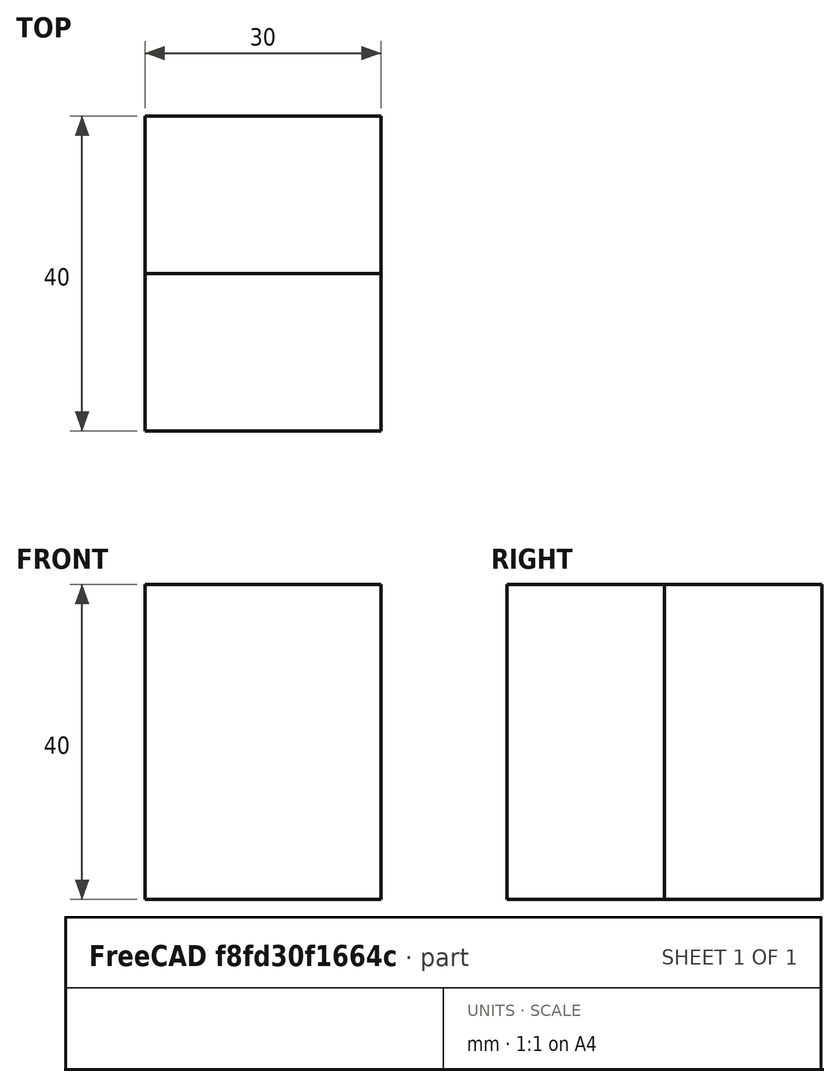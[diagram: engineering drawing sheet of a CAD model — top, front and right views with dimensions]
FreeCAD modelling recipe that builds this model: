
FCSTD DOCUMENT  (FreeCAD 0.17R13509 (Git))
Label: tensor
License: All rights reserved
LicenseURL: http://en.wikipedia.org/wiki/All_rights_reserved
objects: Part::Box×48, Part::MultiFuse×22
note: 70 computed .brp shape members not serialized (recipe doc carries the construction recipe); baked Part::Feature solids carry a one-line shape summary decoded from their .brp

FEATURE [Part::Box] Box021  label="Cube021"
  AttacherType = Attacher::AttachEngine3D
  Height = 10
  Length = 10
  Placement = pos=(34,0,30) rot=(0,0,1;0rad)
  Width = 10
FEATURE [Part::Box] Box022  label="Cube022"
  AttacherType = Attacher::AttachEngine3D
  Height = 10
  Length = 10
  Placement = pos=(14,0,30) rot=(0,0,1;0rad)
  Width = 10
FEATURE [Part::Box] Box023  label="Cube023"
  AttacherType = Attacher::AttachEngine3D
  Height = 10
  Length = 10
  Placement = pos=(14,0,30) rot=(0,0,1;0rad)
  Width = 10
FEATURE [Part::Box] Box024  label="Cube024"
  AttacherType = Attacher::AttachEngine3D
  Height = 10
  Length = 10
  Placement = pos=(24,0,30) rot=(0,0,1;0rad)
  Width = 10
FEATURE [Part::Box] Box025  label="Cube025"
  AttacherType = Attacher::AttachEngine3D
  Height = 10
  Length = 10
  Placement = pos=(24,0,30) rot=(0,0,1;0rad)
  Width = 10
FEATURE [Part::MultiFuse] Fusion012
  Shapes = -> [Box022,Box025,Box021]
FEATURE [Part::Box] Box026  label="Cube026"
  AttacherType = Attacher::AttachEngine3D
  Height = 10
  Length = 10
  Placement = pos=(34,0,30) rot=(0,0,1;0rad)
  Width = 10
FEATURE [Part::MultiFuse] Fusion011
  Placement = pos=(0,0,-10) rot=(0,0,1;0rad)
  Shapes = -> [Box023,Box024,Box026]
FEATURE [Part::Box] Box027  label="Cube027"
  AttacherType = Attacher::AttachEngine3D
  Height = 10
  Length = 10
  Placement = pos=(34,0,30) rot=(0,0,1;0rad)
  Width = 10
FEATURE [Part::Box] Box028  label="Cube028"
  AttacherType = Attacher::AttachEngine3D
  Height = 10
  Length = 10
  Placement = pos=(14,0,30) rot=(0,0,1;0rad)
  Width = 10
FEATURE [Part::Box] Box029  label="Cube029"
  AttacherType = Attacher::AttachEngine3D
  Height = 10
  Length = 10
  Placement = pos=(24,0,30) rot=(0,0,1;0rad)
  Width = 10
FEATURE [Part::MultiFuse] Fusion008
  Placement = pos=(0,0,-20) rot=(0,0,1;0rad)
  Shapes = -> [Box028,Box029,Box027]
FEATURE [Part::Box] Box030  label="Cube030"
  AttacherType = Attacher::AttachEngine3D
  Height = 10
  Length = 10
  Placement = pos=(34,0,30) rot=(0,0,1;0rad)
  Width = 10
FEATURE [Part::Box] Box031  label="Cube031"
  AttacherType = Attacher::AttachEngine3D
  Height = 10
  Length = 10
  Placement = pos=(14,0,30) rot=(0,0,1;0rad)
  Width = 10
FEATURE [Part::Box] Box032  label="Cube032"
  AttacherType = Attacher::AttachEngine3D
  Height = 10
  Length = 10
  Placement = pos=(24,0,30) rot=(0,0,1;0rad)
  Width = 10
FEATURE [Part::MultiFuse] Fusion009
  Placement = pos=(0,0,-30) rot=(0,0,1;0rad)
  Shapes = -> [Box031,Box032,Box030]
FEATURE [Part::MultiFuse] Fusion010  label="Mode013"
  Placement = pos=(0,-14,0) rot=(0,0,1;0rad)
  Shapes = -> [Fusion012,Fusion011,Fusion009,Fusion008]
FEATURE [Part::Box] Box033  label="Cube033"
  AttacherType = Attacher::AttachEngine3D
  Height = 10
  Length = 10
  Placement = pos=(34,0,30) rot=(0,0,1;0rad)
  Width = 10
FEATURE [Part::Box] Box034  label="Cube034"
  AttacherType = Attacher::AttachEngine3D
  Height = 10
  Length = 10
  Placement = pos=(24,0,30) rot=(0,0,1;0rad)
  Width = 10
FEATURE [Part::Box] Box035  label="Cube035"
  AttacherType = Attacher::AttachEngine3D
  Height = 10
  Length = 10
  Placement = pos=(14,0,30) rot=(0,0,1;0rad)
  Width = 10
FEATURE [Part::Box] Box036  label="Cube036"
  AttacherType = Attacher::AttachEngine3D
  Height = 10
  Length = 10
  Placement = pos=(14,0,30) rot=(0,0,1;0rad)
  Width = 10
FEATURE [Part::Box] Box037  label="Cube037"
  AttacherType = Attacher::AttachEngine3D
  Height = 10
  Length = 10
  Placement = pos=(34,0,30) rot=(0,0,1;0rad)
  Width = 10
FEATURE [Part::Box] Box038  label="Cube038"
  AttacherType = Attacher::AttachEngine3D
  Height = 10
  Length = 10
  Placement = pos=(14,0,30) rot=(0,0,1;0rad)
  Width = 10
FEATURE [Part::Box] Box039  label="Cube039"
  AttacherType = Attacher::AttachEngine3D
  Height = 10
  Length = 10
  Placement = pos=(24,0,30) rot=(0,0,1;0rad)
  Width = 10
FEATURE [Part::Box] Box040  label="Cube040"
  AttacherType = Attacher::AttachEngine3D
  Height = 10
  Length = 10
  Placement = pos=(14,0,30) rot=(0,0,1;0rad)
  Width = 10
FEATURE [Part::MultiFuse] Fusion016
  Placement = pos=(0,0,-20) rot=(0,0,1;0rad)
  Shapes = -> [Box040,Box034,Box033]
FEATURE [Part::Box] Box041  label="Cube041"
  AttacherType = Attacher::AttachEngine3D
  Height = 10
  Length = 10
  Placement = pos=(24,0,30) rot=(0,0,1;0rad)
  Width = 10
FEATURE [Part::Box] Box042  label="Cube042"
  AttacherType = Attacher::AttachEngine3D
  Height = 10
  Length = 10
  Placement = pos=(34,0,30) rot=(0,0,1;0rad)
  Width = 10
FEATURE [Part::MultiFuse] Fusion013
  Placement = pos=(0,0,-30) rot=(0,0,1;0rad)
  Shapes = -> [Box036,Box039,Box042]
FEATURE [Part::Box] Box043  label="Cube043"
  AttacherType = Attacher::AttachEngine3D
  Height = 10
  Length = 10
  Placement = pos=(34,0,30) rot=(0,0,1;0rad)
  Width = 10
FEATURE [Part::MultiFuse] Fusion015
  Shapes = -> [Box038,Box041,Box043]
FEATURE [Part::Box] Box044  label="Cube044"
  AttacherType = Attacher::AttachEngine3D
  Height = 10
  Length = 10
  Placement = pos=(24,0,30) rot=(0,0,1;0rad)
  Width = 10
FEATURE [Part::MultiFuse] Fusion017
  Placement = pos=(0,0,-10) rot=(0,0,1;0rad)
  Shapes = -> [Box035,Box044,Box037]
FEATURE [Part::MultiFuse] Fusion014  label="Mode014"
  Placement = pos=(0,-24,0) rot=(0,0,1;0rad)
  Shapes = -> [Fusion015,Fusion017,Fusion013,Fusion016]
FEATURE [Part::MultiFuse] Fusion  label="Mode123"
  Shapes = -> [Fusion014,Fusion010]
FEATURE [Part::Box] Box045  label="Cube045"
  AttacherType = Attacher::AttachEngine3D
  Height = 10
  Length = 10
  Placement = pos=(34,0,30) rot=(0,0,1;0rad)
  Width = 10
FEATURE [Part::Box] Box046  label="Cube046"
  AttacherType = Attacher::AttachEngine3D
  Height = 10
  Length = 10
  Placement = pos=(14,0,30) rot=(0,0,1;0rad)
  Width = 10
FEATURE [Part::Box] Box047  label="Cube047"
  AttacherType = Attacher::AttachEngine3D
  Height = 10
  Length = 10
  Placement = pos=(14,0,30) rot=(0,0,1;0rad)
  Width = 10
FEATURE [Part::Box] Box048  label="Cube048"
  AttacherType = Attacher::AttachEngine3D
  Height = 10
  Length = 10
  Placement = pos=(24,0,30) rot=(0,0,1;0rad)
  Width = 10
FEATURE [Part::Box] Box049  label="Cube049"
  AttacherType = Attacher::AttachEngine3D
  Height = 10
  Length = 10
  Placement = pos=(24,0,30) rot=(0,0,1;0rad)
  Width = 10
FEATURE [Part::MultiFuse] Fusion022
  Shapes = -> [Box046,Box049,Box045]
FEATURE [Part::Box] Box050  label="Cube050"
  AttacherType = Attacher::AttachEngine3D
  Height = 10
  Length = 10
  Placement = pos=(34,0,30) rot=(0,0,1;0rad)
  Width = 10
FEATURE [Part::MultiFuse] Fusion021
  Placement = pos=(0,0,-10) rot=(0,0,1;0rad)
  Shapes = -> [Box047,Box048,Box050]
FEATURE [Part::Box] Box051  label="Cube051"
  AttacherType = Attacher::AttachEngine3D
  Height = 10
  Length = 10
  Placement = pos=(34,0,30) rot=(0,0,1;0rad)
  Width = 10
FEATURE [Part::Box] Box052  label="Cube052"
  AttacherType = Attacher::AttachEngine3D
  Height = 10
  Length = 10
  Placement = pos=(14,0,30) rot=(0,0,1;0rad)
  Width = 10
FEATURE [Part::Box] Box053  label="Cube053"
  AttacherType = Attacher::AttachEngine3D
  Height = 10
  Length = 10
  Placement = pos=(24,0,30) rot=(0,0,1;0rad)
  Width = 10
FEATURE [Part::MultiFuse] Fusion018
  Placement = pos=(0,0,-20) rot=(0,0,1;0rad)
  Shapes = -> [Box052,Box053,Box051]
FEATURE [Part::Box] Box054  label="Cube054"
  AttacherType = Attacher::AttachEngine3D
  Height = 10
  Length = 10
  Placement = pos=(34,0,30) rot=(0,0,1;0rad)
  Width = 10
FEATURE [Part::Box] Box055  label="Cube055"
  AttacherType = Attacher::AttachEngine3D
  Height = 10
  Length = 10
  Placement = pos=(14,0,30) rot=(0,0,1;0rad)
  Width = 10
FEATURE [Part::Box] Box056  label="Cube056"
  AttacherType = Attacher::AttachEngine3D
  Height = 10
  Length = 10
  Placement = pos=(24,0,30) rot=(0,0,1;0rad)
  Width = 10
FEATURE [Part::MultiFuse] Fusion019
  Placement = pos=(0,0,-30) rot=(0,0,1;0rad)
  Shapes = -> [Box055,Box056,Box054]
FEATURE [Part::MultiFuse] Fusion020  label="Mode124"
  Placement = pos=(0,-14,0) rot=(0,0,1;0rad)
  Shapes = -> [Fusion022,Fusion021,Fusion019,Fusion018]
FEATURE [Part::Box] Box057  label="Cube057"
  AttacherType = Attacher::AttachEngine3D
  Height = 10
  Length = 10
  Placement = pos=(34,0,30) rot=(0,0,1;0rad)
  Width = 10
FEATURE [Part::Box] Box058  label="Cube058"
  AttacherType = Attacher::AttachEngine3D
  Height = 10
  Length = 10
  Placement = pos=(24,0,30) rot=(0,0,1;0rad)
  Width = 10
FEATURE [Part::Box] Box059  label="Cube059"
  AttacherType = Attacher::AttachEngine3D
  Height = 10
  Length = 10
  Placement = pos=(14,0,30) rot=(0,0,1;0rad)
  Width = 10
FEATURE [Part::Box] Box060  label="Cube060"
  AttacherType = Attacher::AttachEngine3D
  Height = 10
  Length = 10
  Placement = pos=(14,0,30) rot=(0,0,1;0rad)
  Width = 10
FEATURE [Part::Box] Box061  label="Cube061"
  AttacherType = Attacher::AttachEngine3D
  Height = 10
  Length = 10
  Placement = pos=(34,0,30) rot=(0,0,1;0rad)
  Width = 10
FEATURE [Part::Box] Box062  label="Cube062"
  AttacherType = Attacher::AttachEngine3D
  Height = 10
  Length = 10
  Placement = pos=(14,0,30) rot=(0,0,1;0rad)
  Width = 10
FEATURE [Part::Box] Box063  label="Cube063"
  AttacherType = Attacher::AttachEngine3D
  Height = 10
  Length = 10
  Placement = pos=(24,0,30) rot=(0,0,1;0rad)
  Width = 10
FEATURE [Part::Box] Box064  label="Cube064"
  AttacherType = Attacher::AttachEngine3D
  Height = 10
  Length = 10
  Placement = pos=(14,0,30) rot=(0,0,1;0rad)
  Width = 10
FEATURE [Part::MultiFuse] Fusion026
  Placement = pos=(0,0,-20) rot=(0,0,1;0rad)
  Shapes = -> [Box064,Box058,Box057]
FEATURE [Part::Box] Box065  label="Cube065"
  AttacherType = Attacher::AttachEngine3D
  Height = 10
  Length = 10
  Placement = pos=(24,0,30) rot=(0,0,1;0rad)
  Width = 10
FEATURE [Part::Box] Box066  label="Cube066"
  AttacherType = Attacher::AttachEngine3D
  Height = 10
  Length = 10
  Placement = pos=(34,0,30) rot=(0,0,1;0rad)
  Width = 10
FEATURE [Part::MultiFuse] Fusion023
  Placement = pos=(0,0,-30) rot=(0,0,1;0rad)
  Shapes = -> [Box060,Box063,Box066]
FEATURE [Part::Box] Box067  label="Cube067"
  AttacherType = Attacher::AttachEngine3D
  Height = 10
  Length = 10
  Placement = pos=(34,0,30) rot=(0,0,1;0rad)
  Width = 10
FEATURE [Part::MultiFuse] Fusion025
  Shapes = -> [Box062,Box065,Box067]
FEATURE [Part::Box] Box068  label="Cube068"
  AttacherType = Attacher::AttachEngine3D
  Height = 10
  Length = 10
  Placement = pos=(24,0,30) rot=(0,0,1;0rad)
  Width = 10
FEATURE [Part::MultiFuse] Fusion027
  Placement = pos=(0,0,-10) rot=(0,0,1;0rad)
  Shapes = -> [Box059,Box068,Box061]
FEATURE [Part::MultiFuse] Fusion024  label="Mode125"
  Placement = pos=(0,-24,0) rot=(0,0,1;0rad)
  Shapes = -> [Fusion025,Fusion027,Fusion023,Fusion026]
FEATURE [Part::MultiFuse] Fusion028  label="Mode126"
  Placement = pos=(0,-20,0) rot=(0,0,1;0rad)
  Shapes = -> [Fusion024,Fusion020]
